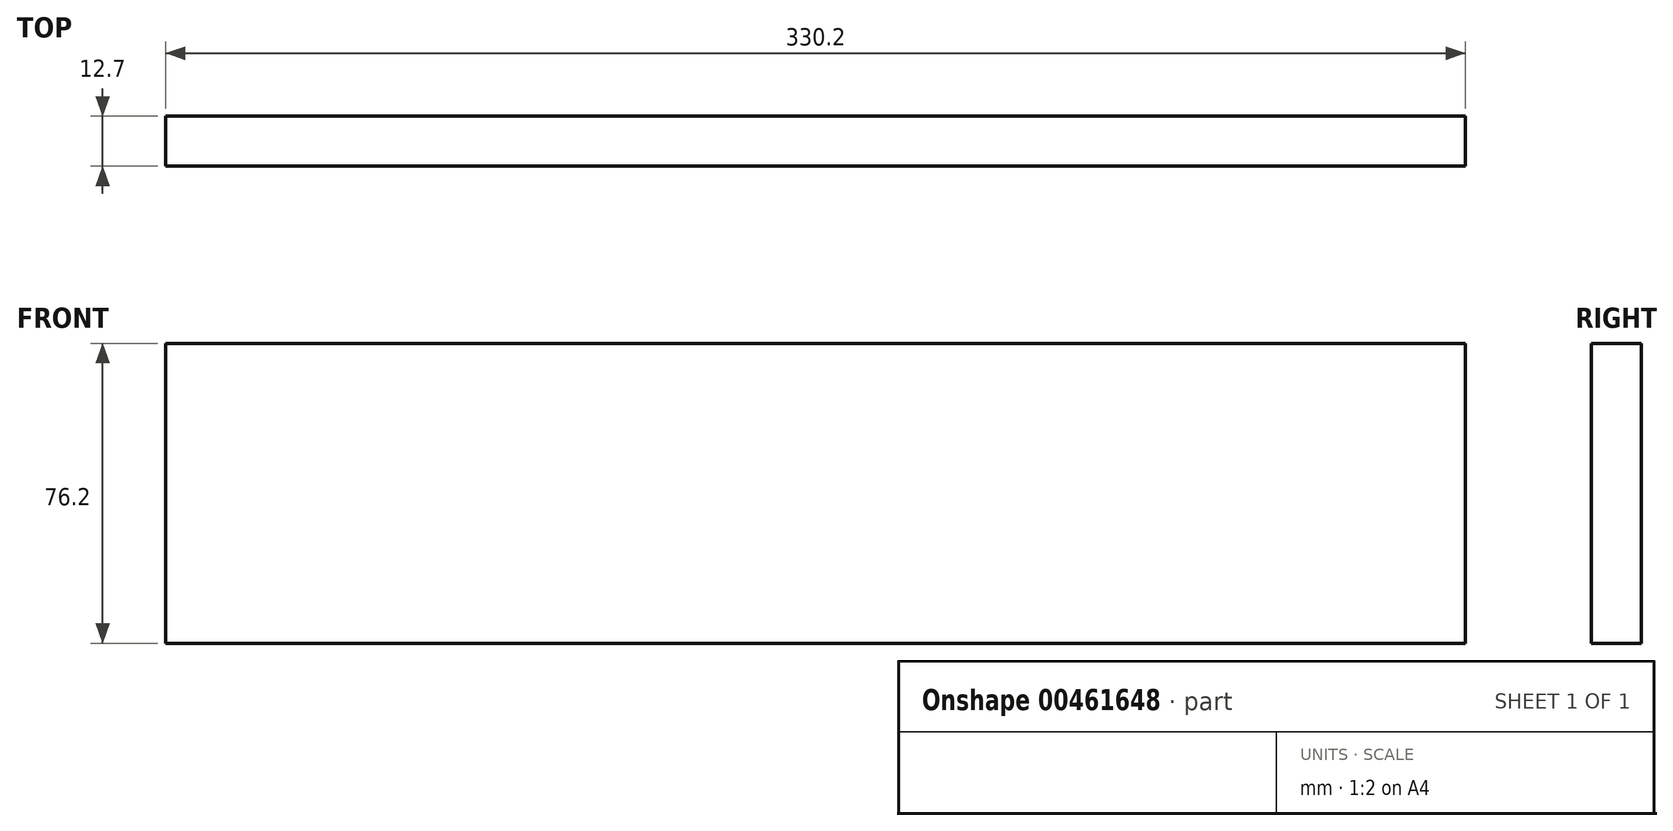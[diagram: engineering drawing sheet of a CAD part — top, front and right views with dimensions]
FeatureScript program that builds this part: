
annotation { "Feature Type Name" : "Feature", "Feature Type Description" : "" }
export const myFeature = defineFeature(function(context is Context, id is Id, definition is map)
    precondition{}
    {
        {
            var Q0;
            Q0=qCreatedBy(makeId("Front.planeOp"),FACE);
            var sketch = newSketch(context, id + "F0", { "sketchPlane" : qUnion([Q0])});
            skLineSegment(sketch, "E0.bottom", {"start": v(165.1, 38.1) * mm, "end": v(-165.1, 38.1) * mm});
            skLineSegment(sketch, "E0.top", {"start": v(165.1, -38.1) * mm, "end": v(-165.1, -38.1) * mm});
            skLineSegment(sketch, "E0.left", {"start": v(165.1, 38.1) * mm, "end": v(165.1, -38.1) * mm});
            skLineSegment(sketch, "E0.right", {"start": v(-165.1, 38.1) * mm, "end": v(-165.1, -38.1) * mm});
            skPoint(sketch, "E0.middle", {"position": v(0, 0) * mm});
            skSolve(sketch);
        }
        {
            var Q0;
            Q0 = qSketchRegion(id + "F0", true);
            extrude(context, id + "F1", {"entities" : qUnion([Q0]), "depth" : 12.7 * mm});
        }
    });
